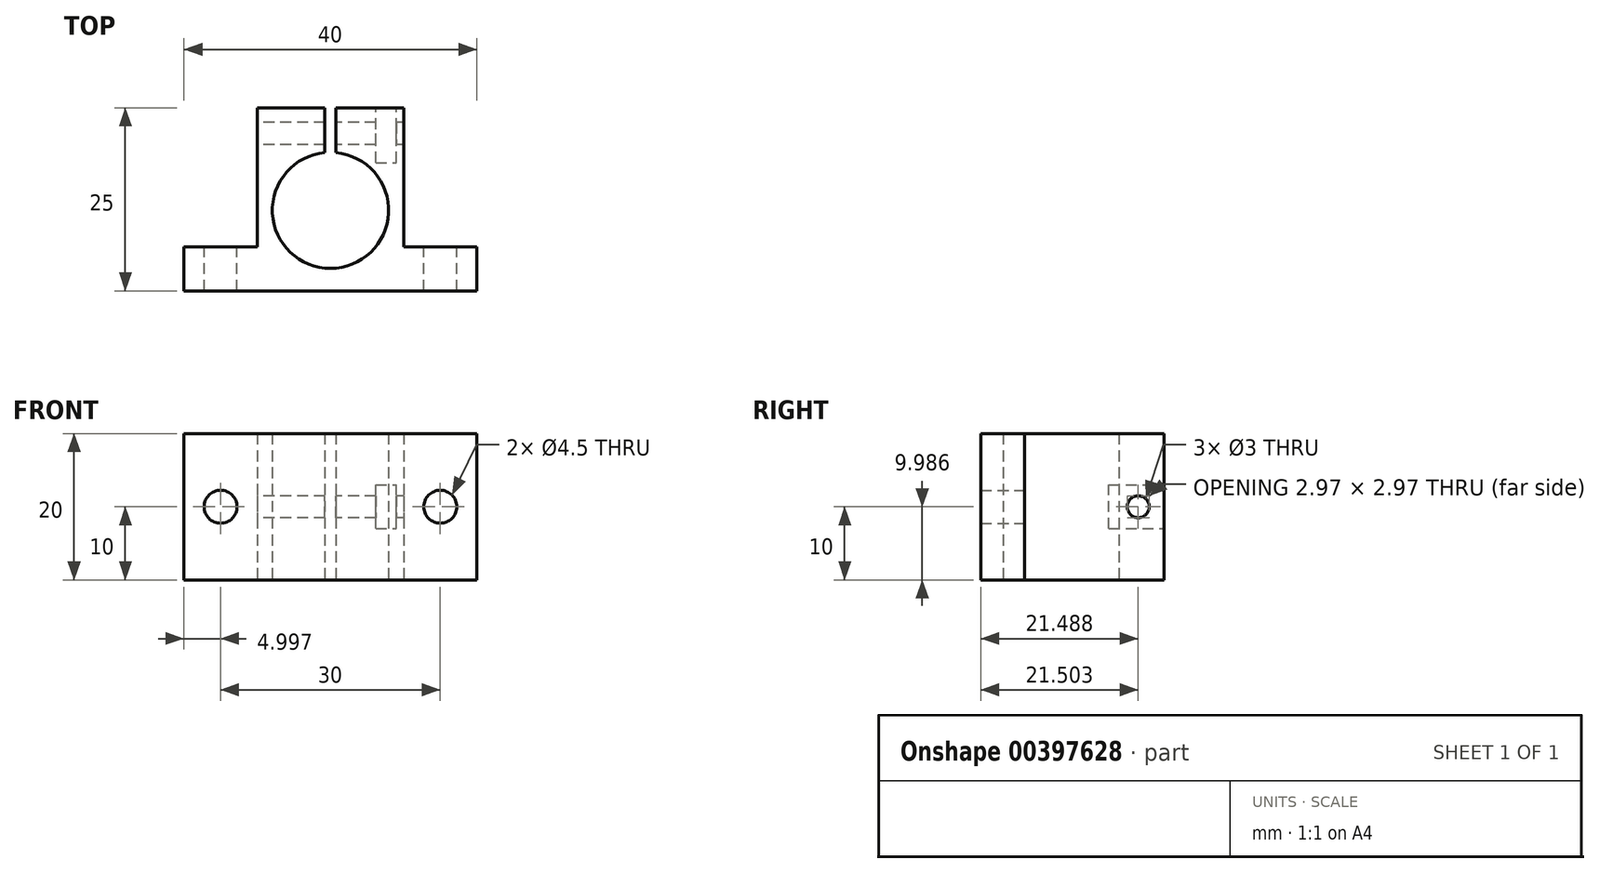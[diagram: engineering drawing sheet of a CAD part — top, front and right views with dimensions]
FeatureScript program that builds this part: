
annotation { "Feature Type Name" : "Feature", "Feature Type Description" : "" }
export const myFeature = defineFeature(function(context is Context, id is Id, definition is map)
    precondition{}
    {
        {
            var Q0;
            Q0=qCreatedBy(makeId("Top.planeOp"),FACE);
            var sketch = newSketch(context, id + "F0", { "sketchPlane" : qUnion([Q0])});
            skLineSegment(sketch, "E0.left", {"start": v(-48.33, -11.35) * mm, "end": v(-48.33, -5.35) * mm});
            skLineSegment(sketch, "E1.bottom", {"start": v(-38.33, -5.35) * mm, "end": v(-18.33, -5.35) * mm});
            skLineSegment(sketch, "E1.top", {"start": v(-38.33, 13.65) * mm, "end": v(-18.33, 13.65) * mm});
            skLineSegment(sketch, "E1.left", {"start": v(-38.33, -5.35) * mm, "end": v(-38.33, 13.65) * mm});
            skLineSegment(sketch, "E1.right", {"start": v(-18.33, -5.35) * mm, "end": v(-18.33, 13.65) * mm});
            skLineSegment(sketch, "E2", {"start": v(-8.33, -5.35) * mm, "end": v(-8.33, -11.35) * mm});
            skCircle(sketch, "E3", {"center": v(-28.33, -0.35) * mm, "radius": 7.94 * mm});
            skLineSegment(sketch, "E4.bottom", {"start": v(-29.08, 13.65) * mm, "end": v(-27.58, 13.65) * mm});
            skLineSegment(sketch, "E4.top", {"start": v(-29.08, -0.35) * mm, "end": v(-27.58, -0.35) * mm});
            skLineSegment(sketch, "E4.left", {"start": v(-29.08, 13.65) * mm, "end": v(-29.08, -0.35) * mm});
            skLineSegment(sketch, "E4.right", {"start": v(-27.58, 13.65) * mm, "end": v(-27.58, -0.35) * mm});
            skLineSegment(sketch, "E5", {"start": v(-48.33, -5.35) * mm, "end": v(-8.33, -5.35) * mm});
            skLineSegment(sketch, "E6", {"start": v(-8.33, -11.35) * mm, "end": v(-48.33, -11.35) * mm});
            skSolve(sketch);
        }
        {
            var Q0;
            {var subQ2=sQuery(id+"F0.wireOp",EDGE,"E1.left");Q0=makeQuery(id+"F0.imprint","IMPRINT",FACE,{"disambiguationData":[TD([[makeQuery(id+"F0.imprint","IMPRINT",EDGE,{"derivedFrom":subQ2}),-1.0]])]});}
            var Q1;
            {var subQ1=sQuery(id+"F0.wireOp",EDGE,"E0.left");Q1=makeQuery(id+"F0.imprint","IMPRINT",FACE,{"disambiguationData":[TD([[makeQuery(id+"F0.imprint","IMPRINT",EDGE,{"derivedFrom":subQ1}),-1.0]])]});}
            var Q2;
            {var subQ7=sQuery(id+"F0.wireOp",EDGE,"E1.right");Q2=makeQuery(id+"F0.imprint","IMPRINT",FACE,{"disambiguationData":[TD([[makeQuery(id+"F0.imprint","IMPRINT",EDGE,{"derivedFrom":subQ7}),1.0]])]});}
            extrude(context, id + "F1", {"entities" : qUnion([Q0, Q1, Q2]), "depth" : 20 * mm, "offsetDistance" : 25 * mm});
        }
        {
            var Q0;
            Q0=makeQuery(id+"F1.opExtrude","SWEPT_FACE",FACE,{"disambiguationData":[OSD([sQuery(id+"F0.wireOp",EDGE,"E1.left")])]});
            var sketch = newSketch(context, id + "F2", { "sketchPlane" : qUnion([Q0])});
            skCircle(sketch, "E7", {"center": v(-10.15, 10) * mm, "radius": 1.5 * mm});
            skSolve(sketch);
        }
        {
            var Q0;
            Q0=qSketchRegion(id+"F2",true);
            extrude(context, id + "F3", {"entities" : qUnion([Q0]), "operationType" : NewBodyOperationType.REMOVE, "oppositeDirection" : true, "depth" : 20 * mm});
        }
        {
            var Q0;
            {var subQ0=sQuery(id+"F0.wireOp",EDGE,"E1.top");Q0=makeQuery(id+"F1.opExtrude","SWEPT_FACE",FACE,{"disambiguationData":[OSD([subQ0]),TDD([makeQuery(id+"F0.imprint","IMPRINT",EDGE,{"disambiguationData":[TD([[makeQuery(id+"F0.imprint","INTERSECT",VERTEX,{"derivedFrom":[subQ0,sQuery(id+"F0.wireOp",EDGE,"E1.left")]}),-1.0]])],"derivedFrom":subQ0})])]});}
            var sketch = newSketch(context, id + "F4", { "sketchPlane" : qUnion([Q0])});
            skLineSegment(sketch, "E8.bottom", {"start": v(22.13, 7) * mm, "end": v(19.33, 7) * mm});
            skLineSegment(sketch, "E8.top", {"start": v(22.13, 13) * mm, "end": v(19.33, 13) * mm});
            skLineSegment(sketch, "E8.left", {"start": v(22.13, 7) * mm, "end": v(22.13, 13) * mm});
            skLineSegment(sketch, "E8.right", {"start": v(19.33, 7) * mm, "end": v(19.33, 13) * mm});
            skSolve(sketch);
        }
        {
            var Q0;
            Q0=qSketchRegion(id+"F4",true);
            extrude(context, id + "F5", {"entities" : qUnion([Q0]), "operationType" : NewBodyOperationType.REMOVE, "oppositeDirection" : true, "depth" : 7.5 * mm});
        }
        {
            var Q0;
            {var subQ0=sQuery(id+"F0.wireOp",EDGE,"E5");Q0=makeQuery(id+"F1.opExtrude","SWEPT_FACE",FACE,{"disambiguationData":[OSD([subQ0]),TDD([makeQuery(id+"F0.imprint","IMPRINT",EDGE,{"disambiguationData":[TD([[makeQuery(id+"F0.imprint","INTERSECT",VERTEX,{"derivedFrom":[sQuery(id+"F0.wireOp",EDGE,"E0.left"),subQ0]}),-1.0]])],"derivedFrom":subQ0})])]});}
            var sketch = newSketch(context, id + "F6", { "sketchPlane" : qUnion([Q0])});
            skCircle(sketch, "E9", {"center": v(43.33, 10) * mm, "radius": 2.25 * mm});
            skLineSegment(sketch, "E10", {"start": v(28.33, 0) * mm, "end": v(28.33, 13.82) * mm});
            skCircle(sketch, "E11.MirrorC", {"center": v(13.33, 10) * mm, "radius": 2.25 * mm});
            skSolve(sketch);
        }
        {
            var Q0;
            Q0=qSketchRegion(id+"F6",true);
            extrude(context, id + "F7", {"entities" : qUnion([Q0]), "operationType" : NewBodyOperationType.REMOVE, "oppositeDirection" : true, "depth" : 6 * mm});
        }
    });
